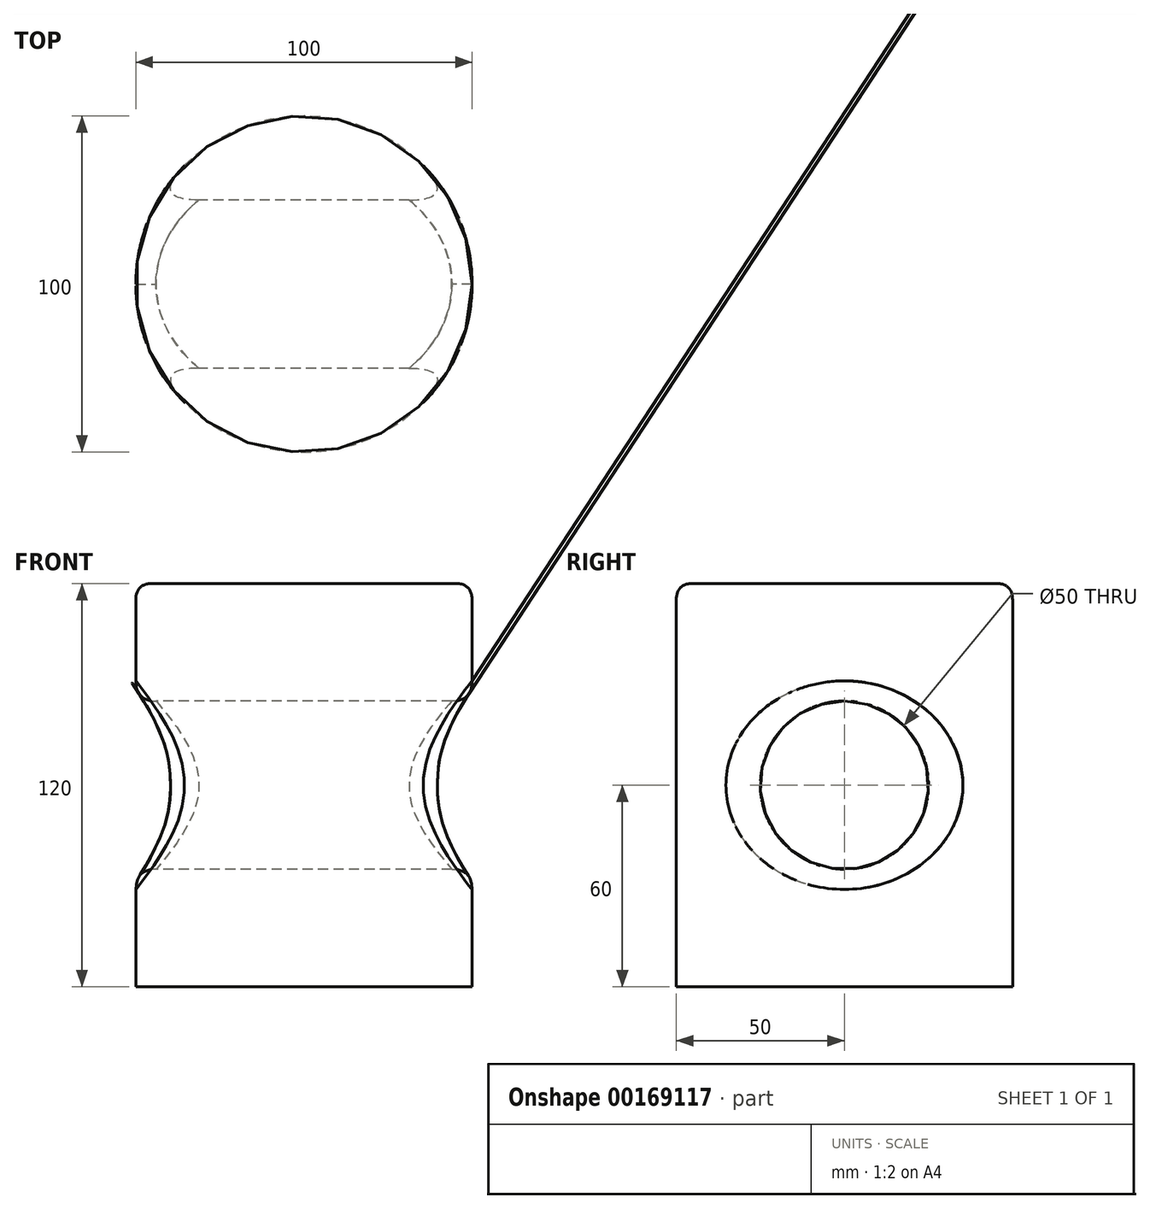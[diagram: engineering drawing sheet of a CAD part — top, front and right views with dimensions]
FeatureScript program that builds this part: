
annotation { "Feature Type Name" : "Feature", "Feature Type Description" : "" }
export const myFeature = defineFeature(function(context is Context, id is Id, definition is map)
    precondition{}
    {
        {
            var Q0;
            Q0=qCreatedBy(makeId("Top.planeOp"),FACE);
            var sketch = newSketch(context, id + "F0", { "sketchPlane" : qUnion([Q0])});
            skCircle(sketch, "E0", {"center": v(0, 0) * mm, "radius": 50 * mm});
            skSolve(sketch);
        }
        {
            var Q0;
            Q0 = qSketchRegion(id + "F0", true);
            extrude(context, id + "F1", {"entities" : qUnion([Q0]), "depth" : 120 * mm});
        }
        {
            var Q0;
            Q0=qCreatedBy(makeId("Right.planeOp"),FACE);
            var sketch = newSketch(context, id + "F2", { "sketchPlane" : qUnion([Q0])});
            skCircle(sketch, "E1", {"center": v(0, 60) * mm, "radius": 25 * mm});
            skLineSegment(sketch, "E2", {"start": v(0, 120) * mm, "end": v(0, 0) * mm, "construction": true});
            skSolve(sketch);
        }
        {
            var Q0;
            Q0 = qSketchRegion(id + "F2", true);
            extrude(context, id + "F3", {"entities" : qUnion([Q0]), "operationType" : NewBodyOperationType.REMOVE, "endBound" : BoundingType.SYMMETRIC, "depth" : 200 * mm});
        }
        {
            var Q0;
            Q0=makeQuery(id+"F1.opExtrude","CAP_FACE",FACE,{"disambiguationData":[OSD([sQuery(id+"F0.wireOp",EDGE,"E0")])],"isStart":false});
            fillet(context, id + "F4", {"entities" : qUnion([Q0]), "radius" : 5 * mm, "tangentPropagation" : true, "rho" : 0.5, "crossSection" : FilletCrossSection.CONIC, "allowEdgeOverflow" : false});
        }
        {
            var Q0;
            Q0=makeQuery(id+"F3.boolean.opBoolean","COPY",FACE,{"derivedFrom":makeQuery(id+"F3.opExtrude","SWEPT_FACE",FACE,{"disambiguationData":[OSD([sQuery(id+"F2.wireOp",EDGE,"E1")])]})});
            fillet(context, id + "F5", {"entities" : qUnion([Q0]), "radius" : 6 * mm, "tangentPropagation" : true, "rho" : 0.5, "crossSection" : FilletCrossSection.CONIC, "allowEdgeOverflow" : false});
        }
    });
